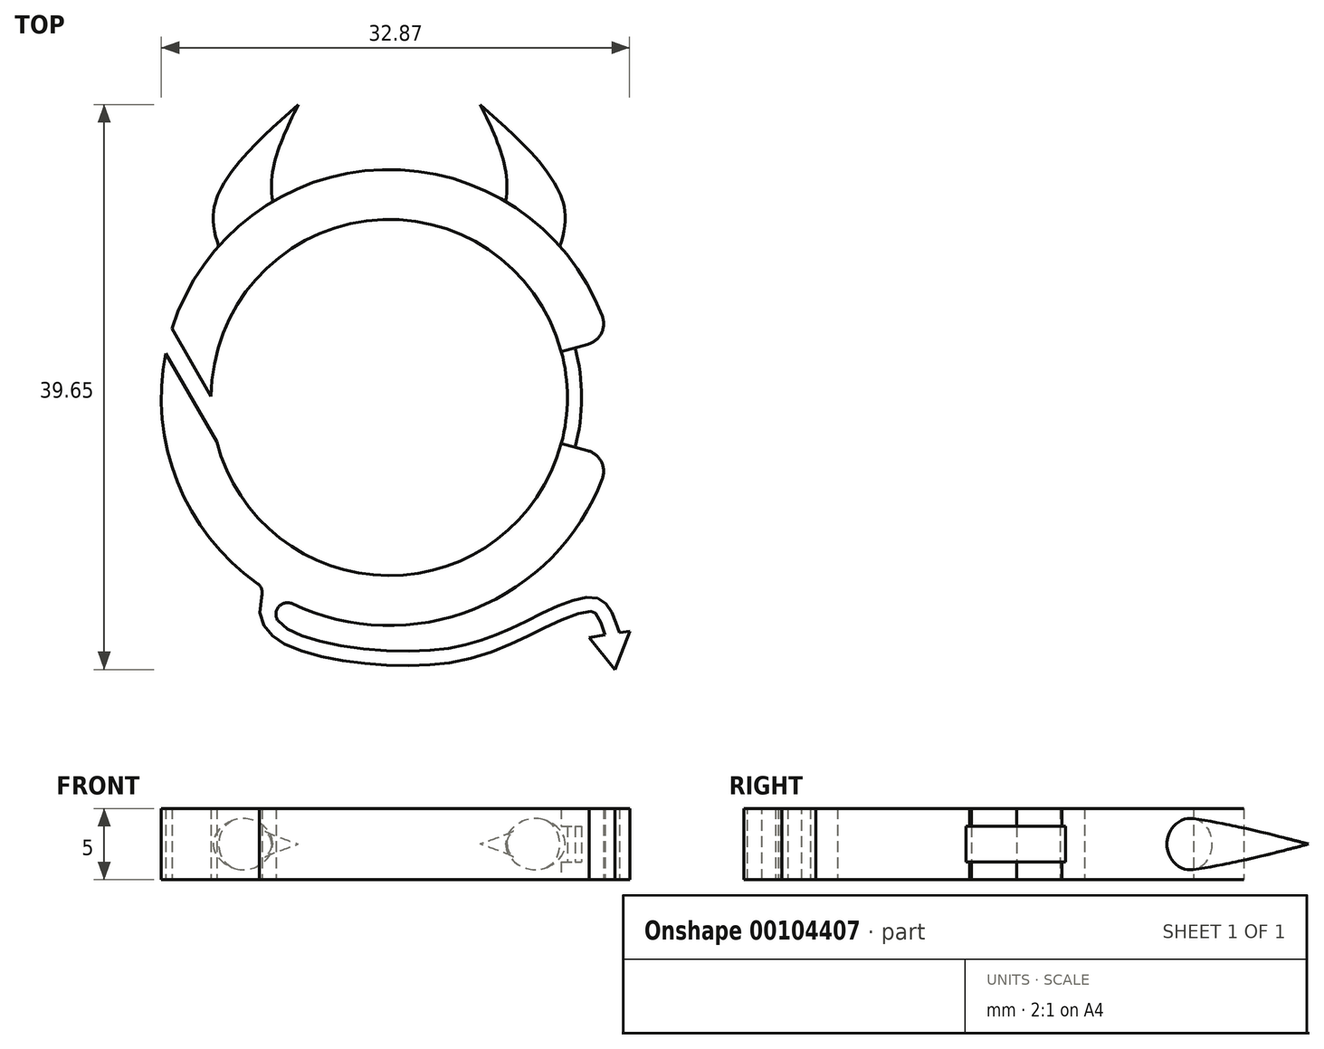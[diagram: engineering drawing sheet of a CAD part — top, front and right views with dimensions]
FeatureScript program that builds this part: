
annotation { "Feature Type Name" : "Feature", "Feature Type Description" : "" }
export const myFeature = defineFeature(function(context is Context, id is Id, definition is map)
    precondition{}
    {
        {
            var Q0;
            Q0=qCreatedBy(makeId("Top.planeOp"),FACE);
            var sketch = newSketch(context, id + "F0", { "sketchPlane" : qUnion([Q0])});
            skCircle(sketch, "E0", {"center": v(0, 0) * mm, "radius": 12.5 * mm});
            skLineSegment(sketch, "E1", {"start": v(12.07, 3.24) * mm, "end": v(15.45, 4.14) * mm});
            skLineSegment(sketch, "E2.MirrorCS", {"start": v(12.07, -3.24) * mm, "end": v(15.45, -4.14) * mm});
            skPoint(sketch, "E3", {"position": v(12.07, 3.24) * mm});
            skPoint(sketch, "E4", {"position": v(12.07, -3.24) * mm});
            skArc(sketch, "E5", {"start": v(13.04, -3.5) * mm, "mid": v(13.5, 0) * mm, "end": v(13.04, 3.5) * mm});
            skLineSegment(sketch, "E6", {"start": v(13.04, 3.5) * mm, "end": v(13.21, 2.76) * mm, "construction": true});
            skLineSegment(sketch, "E7", {"start": v(-16, 0) * mm, "end": v(-12.5, 0) * mm, "construction": true});
            skArc(sketch, "E8", {"start": v(7.61, 15.66) * mm, "mid": v(9.62, 16.68) * mm, "end": v(10.98, 18.48) * mm});
            skArc(sketch, "E9", {"start": v(10.43, 14.02) * mm, "mid": v(11.16, 16.2) * mm, "end": v(10.98, 18.48) * mm});
            skArc(sketch, "E10.MirrorCS", {"start": v(-7.61, 15.66) * mm, "mid": v(-9.62, 16.68) * mm, "end": v(-10.98, 18.48) * mm});
            skArc(sketch, "E11.MirrorCS", {"start": v(-10.43, 14.02) * mm, "mid": v(-11.16, 16.2) * mm, "end": v(-10.98, 18.48) * mm});
            skPoint(sketch, "E12", {"position": v(-10.98, 18.48) * mm});
            skPoint(sketch, "E13", {"position": v(-7.61, 15.66) * mm});
            skPoint(sketch, "E14", {"position": v(-10.43, 14.02) * mm});
            skPoint(sketch, "E15", {"position": v(10.98, 18.48) * mm});
            skPoint(sketch, "E16", {"position": v(7.61, 15.66) * mm});
            skPoint(sketch, "E17", {"position": v(10.43, 14.02) * mm});
            skPoint(sketch, "E18", {"position": v(11.16, 16.2) * mm});
            skPoint(sketch, "E19", {"position": v(9.62, 16.68) * mm});
            skPoint(sketch, "E20", {"position": v(-9.62, 16.68) * mm});
            skPoint(sketch, "E21", {"position": v(-11.16, 16.2) * mm});
            skCircle(sketch, "E22", {"center": v(0, 0) * mm, "radius": 16 * mm});
            skLineSegment(sketch, "E23", {"start": v(-12.1, -3.1) * mm, "end": v(-15.7, 3.1) * mm});
            skLineSegment(sketch, "E24", {"start": v(-12.1, -3.1) * mm, "end": v(-12.1, 3.1) * mm, "construction": true});
            skLineSegment(sketch, "E25", {"start": v(-15.7, 3.1) * mm, "end": v(-15.7, -3.1) * mm, "construction": true});
            skLineSegment(sketch, "E26", {"start": v(-12.1, -0.6) * mm, "end": v(-15.25, 4.84) * mm});
            skFitSpline(sketch, "E27", {"points": [v(-7.81, -13.96) * mm, v(-7.62, -15.88) * mm, v(2.28, -17.78) * mm, v(9.38, -15.8) * mm, v(14.77, -14.14) * mm, v(16.14, -16.51) * mm], "startDerivative": vector(-8.6, -14.32) * mm, "endDerivative": vector(5.66, -16.46) * mm});
            skFitSpline(sketch, "E28.0", {"points": [v(-8.67, -13.45) * mm, v(-8.8, -13.67) * mm, v(-9.02, -14.14) * mm, v(-9.11, -14.84) * mm, v(-9.02, -15.44) * mm, v(-8.86, -15.88) * mm, v(-8.6, -16.3) * mm, v(-8.27, -16.66) * mm, v(-7.88, -16.96) * mm, v(-7.31, -17.31) * mm, v(-6.5, -17.67) * mm, v(-5.4, -18.02) * mm, v(-4.17, -18.3) * mm, v(-2.86, -18.52) * mm, v(-1.5, -18.68) * mm, v(-0.14, -18.78) * mm, v(1.19, -18.81) * mm, v(2.45, -18.78) * mm, v(3.61, -18.7) * mm, v(4.68, -18.53) * mm, v(6.02, -18.25) * mm, v(7.24, -17.85) * mm, v(8.42, -17.36) * mm, v(9.29, -16.96) * mm, v(10.18, -16.53) * mm, v(11.08, -16.08) * mm, v(11.96, -15.66) * mm, v(12.78, -15.32) * mm, v(13.5, -15.08) * mm, v(13.97, -15) * mm, v(14.22, -15.01) * mm, v(14.32, -15.03) * mm, v(14.36, -15.05) * mm, v(14.38, -15.06) * mm, v(14.43, -15.1) * mm, v(14.51, -15.18) * mm, v(14.65, -15.36) * mm, v(14.82, -15.72) * mm, v(15.01, -16.26) * mm, v(15.13, -16.64) * mm, v(15.2, -16.84) * mm]});
            skFitSpline(sketch, "E29", {"points": [v(12.74, -15.35) * mm, v(14.05, -15.08) * mm, v(14.72, -15.74) * mm, v(14.84, -16.72) * mm], "startDerivative": vector(2.92, 0.98) * mm, "endDerivative": vector(0.86, -2.3) * mm});
            skLineSegment(sketch, "E30", {"start": v(14.03, -16.85) * mm, "end": v(16.87, -16.4) * mm});
            skLineSegment(sketch, "E31", {"start": v(14.03, -16.85) * mm, "end": v(15.85, -19.09) * mm});
            skLineSegment(sketch, "E32", {"start": v(15.85, -19.09) * mm, "end": v(16.87, -16.4) * mm});
            skSolve(sketch);
        }
        {
            var Q0;
            {var subQ1=sQuery(id+"F0.wireOp",EDGE,"E1");var subQ6=sQuery(id+"F0.wireOp",EDGE,"E0");var subQ7=makeQuery(id+"F0.imprint","INTERSECT",VERTEX,{"derivedFrom":[subQ6,subQ1]});Q0=makeQuery(id+"F0.imprint","IMPRINT",FACE,{"disambiguationData":[TD([[makeQuery(id+"F0.imprint","IMPRINT",EDGE,{"disambiguationData":[TD([[subQ7,-1.0]])],"derivedFrom":subQ6}),-1.0]])]});}
            var Q1;
            {var subQ3=sQuery(id+"F0.wireOp",EDGE,"E23");Q1=makeQuery(id+"F0.imprint","IMPRINT",FACE,{"disambiguationData":[TD([[makeQuery(id+"F0.imprint","IMPRINT",EDGE,{"derivedFrom":subQ3}),1.0]])]});}
            var Q2;
            {var subQ2=sQuery(id+"F0.wireOp",EDGE,"E27");Q2=makeQuery(id+"F0.imprint","IMPRINT",FACE,{"disambiguationData":[TD([[makeQuery(id+"F0.imprint","IMPRINT",EDGE,{"derivedFrom":subQ2}),-1.0]])]});}
            var Q3;
            {var subQ0=sQuery(id+"F0.wireOp",EDGE,"E31");Q3=makeQuery(id+"F0.imprint","IMPRINT",FACE,{"disambiguationData":[TD([[makeQuery(id+"F0.imprint","IMPRINT",EDGE,{"derivedFrom":subQ0}),1.0]])]});}
            extrude(context, id + "F1", {"entities" : qUnion([Q0, Q1, Q2, Q3]), "endBound" : BoundingType.SYMMETRIC, "depth" : 5 * mm});
        }
        {
            var Q0;
            {var subQ5=sQuery(id+"F0.wireOp",EDGE,"E5");Q0=makeQuery(id+"F0.imprint","IMPRINT",FACE,{"disambiguationData":[TD([[makeQuery(id+"F0.imprint","IMPRINT",EDGE,{"derivedFrom":subQ5}),1.0]])]});}
            extrude(context, id + "F2", {"entities" : qUnion([Q0]), "operationType" : NewBodyOperationType.ADD, "endBound" : BoundingType.SYMMETRIC, "depth" : 2.5 * mm});
        }
        {
            var Q0;
            Q0=makeQuery(id+"F1.opExtrude","SWEPT_EDGE",EDGE,{"disambiguationData":[OSD([sQuery(id+"F0.wireOp",EDGE,"E2.MirrorCS"),sQuery(id+"F0.wireOp",EDGE,"E22")])]});
            var Q1;
            Q1=makeQuery(id+"F1.opExtrude","SWEPT_EDGE",EDGE,{"disambiguationData":[OSD([sQuery(id+"F0.wireOp",EDGE,"E2.MirrorCS"),sQuery(id+"F0.wireOp",EDGE,"E22")])]});
            var Q2;
            Q2=makeQuery(id+"F1.opExtrude","SWEPT_EDGE",EDGE,{"disambiguationData":[OSD([sQuery(id+"F0.wireOp",EDGE,"E1"),sQuery(id+"F0.wireOp",EDGE,"E22")])]});
            var Q3;
            Q3=makeQuery(id+"F1.opExtrude","SWEPT_EDGE",EDGE,{"disambiguationData":[OSD([sQuery(id+"F0.wireOp",EDGE,"E1"),sQuery(id+"F0.wireOp",EDGE,"E22")])]});
            var Q4;
            Q4=makeQuery(id+"F1.opExtrude","SWEPT_EDGE",EDGE,{"disambiguationData":[OSD([sQuery(id+"F0.wireOp",EDGE,"E2.MirrorCS"),sQuery(id+"F0.wireOp",EDGE,"E22")])]});
            fillet(context, id + "F3", {"entities" : qUnion([Q0, Q1, Q2, Q3, Q4]), "radius" : 1.5 * mm, "tangentPropagation" : true, "allowEdgeOverflow" : false});
        }
        {
            var Q0;
            Q0=qCreatedBy(makeId("Front.planeOp"),FACE);
            cPlane(context, id + "F4", {"entities" : qUnion([Q0]), "cplaneType" : CPlaneType.OFFSET, "offset" : 9 * mm, "oppositeDirection" : true, "width" : 150 * mm, "height" : 150 * mm});
        }
        {
            var Q0;
            Q0=qCreatedBy(id+"F4.planeOp",FACE);
            var sketch = newSketch(context, id + "F5", { "sketchPlane" : qUnion([Q0])});
            skEllipse(sketch, "E33", {"center": v(-8.31, 0) * mm, "majorRadius": 3 * mm, "minorRadius": 2.2 * mm, "majorAxis": v(-1, 0)});
            skEllipse(sketch, "E34.MirrorC", {"center": v(8.31, 0) * mm, "majorRadius": 3 * mm, "minorRadius": 2.2 * mm, "majorAxis": v(1, 0)});
            skSolve(sketch);
        }
        {
            var Q0;
            Q0=qCreatedBy(makeId("Front.planeOp"),FACE);
            cPlane(context, id + "F6", {"entities" : qUnion([Q0]), "cplaneType" : CPlaneType.OFFSET, "offset" : 13 * mm, "oppositeDirection" : true, "width" : 150 * mm, "height" : 150 * mm});
        }
        {
            var Q0;
            Q0=qCreatedBy(id+"F6.planeOp",FACE);
            var sketch = newSketch(context, id + "F7", { "sketchPlane" : qUnion([Q0])});
            skPoint(sketch, "E35", {"position": v(11.16, 0) * mm});
            skPoint(sketch, "E36", {"position": v(9.62, 0) * mm});
            skEllipse(sketch, "E37", {"center": v(-10.15, 0) * mm, "majorRadius": 2.19 * mm, "minorRadius": 1.71 * mm, "majorAxis": v(-1, 0)});
            skEllipse(sketch, "E38.MirrorC", {"center": v(10.15, 0) * mm, "majorRadius": 2.19 * mm, "minorRadius": 1.71 * mm, "majorAxis": v(1, 0)});
            skSolve(sketch);
        }
        {
            var Q1;
            Q1=makeQuery(id+"F5.imprint","IMPRINT",FACE,{"disambiguationData":[TD([[makeQuery(id+"F5.imprint","IMPRINT",EDGE,{"derivedFrom":sQuery(id+"F5.wireOp",EDGE,"E33")}),1.0]])]});
            var Q2;
            Q2=makeQuery(id+"F7.imprint","IMPRINT",FACE,{"disambiguationData":[TD([[makeQuery(id+"F7.imprint","IMPRINT",EDGE,{"derivedFrom":sQuery(id+"F7.wireOp",EDGE,"E37")}),1.0]])]});
            var Q3;
            Q3=sQuery(id+"F0.wireOp",VERTEX,"E10.MirrorCS.center");
            loft(context, id + "F8", {"operationType" : NewBodyOperationType.ADD, "sheetProfilesArray" : [{ "sheetProfileEntities" : qUnion([Q1]) }, { "sheetProfileEntities" : qUnion([Q2]) }, { "sheetProfileEntities" : qUnion([Q3]) }]});
        }
        {
            var Q1;
            Q1=makeQuery(id+"F5.imprint","IMPRINT",FACE,{"disambiguationData":[TD([[makeQuery(id+"F5.imprint","IMPRINT",EDGE,{"derivedFrom":sQuery(id+"F5.wireOp",EDGE,"E34.MirrorC")}),1.0]])]});
            var Q2;
            Q2=makeQuery(id+"F7.imprint","IMPRINT",FACE,{"disambiguationData":[TD([[makeQuery(id+"F7.imprint","IMPRINT",EDGE,{"derivedFrom":sQuery(id+"F7.wireOp",EDGE,"E38.MirrorC")}),1.0]])]});
            var Q3;
            Q3=sQuery(id+"F0.wireOp",VERTEX,"E8.center");
            loft(context, id + "F9", {"operationType" : NewBodyOperationType.ADD, "sheetProfilesArray" : [{ "sheetProfileEntities" : qUnion([Q1]) }, { "sheetProfileEntities" : qUnion([Q2]) }, { "sheetProfileEntities" : qUnion([Q3]) }]});
        }
        {
            var Q0;
            {var subQ0=sQuery(id+"F0.wireOp",EDGE,"E0");var subQ1=makeQuery(id+"F0.imprint","INTERSECT",VERTEX,{"derivedFrom":[subQ0,sQuery(id+"F0.wireOp",EDGE,"E1")]});Q0=makeQuery(id+"F0.imprint","IMPRINT",FACE,{"disambiguationData":[TD([[makeQuery(id+"F0.imprint","IMPRINT",EDGE,{"disambiguationData":[TD([[subQ1,-1.0]])],"derivedFrom":subQ0}),1.0]])]});}
            extrude(context, id + "F10", {"entities" : qUnion([Q0]), "operationType" : NewBodyOperationType.REMOVE, "endBound" : BoundingType.SYMMETRIC, "oppositeDirection" : true, "depth" : 5 * mm});
        }
        {
            var Q0;
            Q0=makeQuery(id+"F1.opExtrude","SWEPT_EDGE",EDGE,{"disambiguationData":[OSD([sQuery(id+"F0.wireOp",EDGE,"E22"),sQuery(id+"F0.wireOp",EDGE,"E27")])]});
            var Q1;
            Q1=makeQuery(id+"F1.opExtrude","SWEPT_EDGE",EDGE,{"disambiguationData":[OSD([sQuery(id+"F0.wireOp",EDGE,"E22"),sQuery(id+"F0.wireOp",EDGE,"E28.0")])]});
            fillet(context, id + "F11", {"entities" : qUnion([Q0, Q1]), "radius" : 0.8 * mm, "tangentPropagation" : true, "allowEdgeOverflow" : false});
        }
    });
